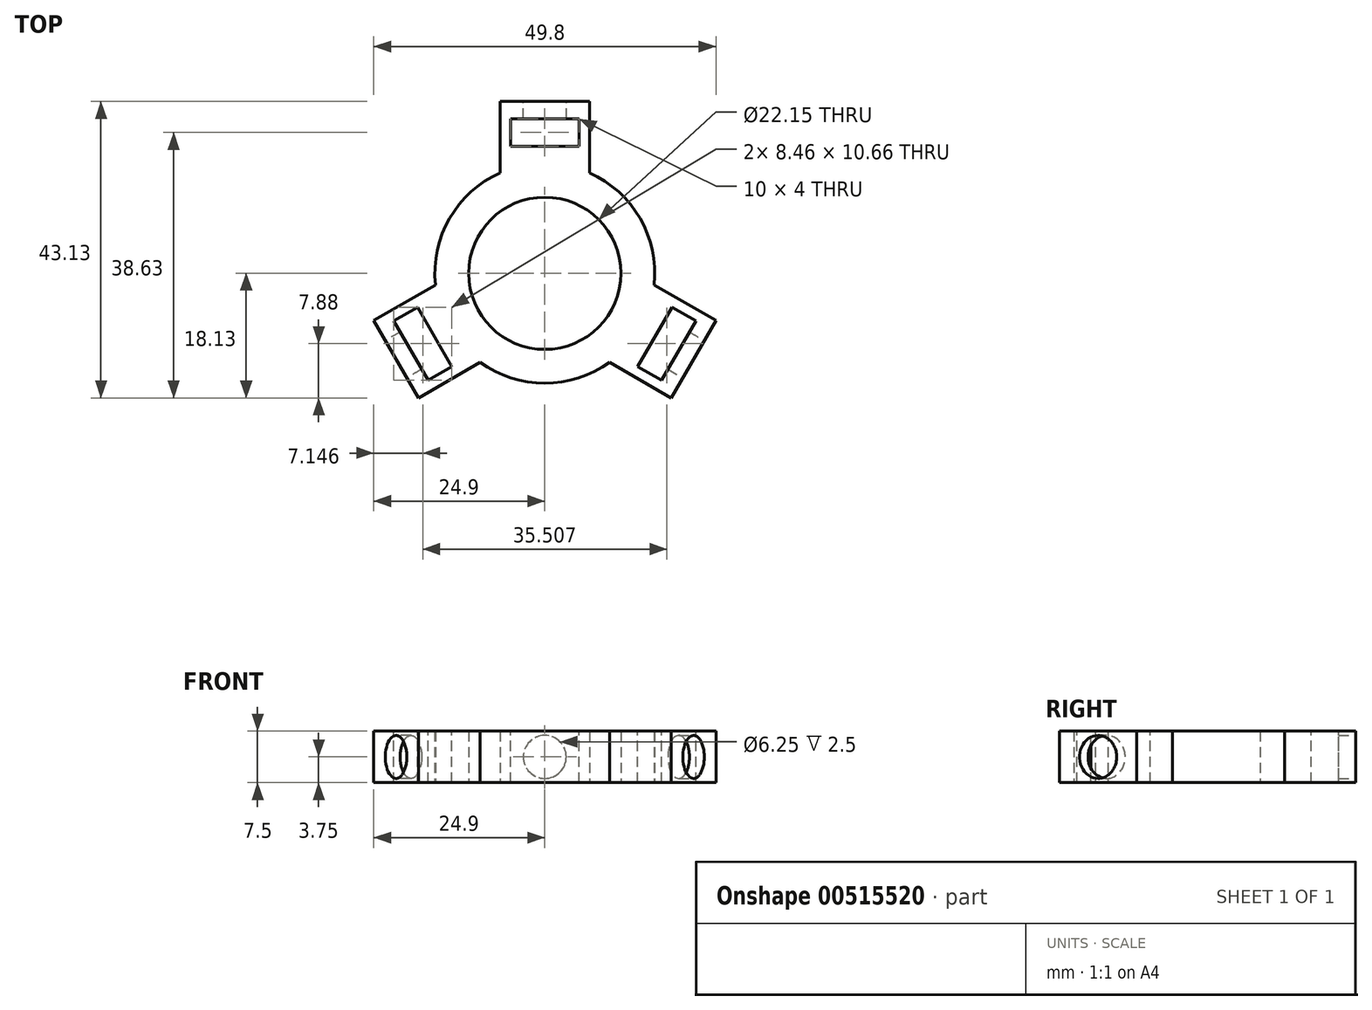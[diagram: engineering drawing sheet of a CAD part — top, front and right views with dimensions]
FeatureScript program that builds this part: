
annotation { "Feature Type Name" : "Feature", "Feature Type Description" : "" }
export const myFeature = defineFeature(function(context is Context, id is Id, definition is map)
    precondition{}
    {
        {
            var Q0;
            Q0=qCreatedBy(makeId("Top.planeOp"),FACE);
            var sketch = newSketch(context, id + "F0", { "sketchPlane" : qUnion([Q0])});
            skCircle(sketch, "E0", {"center": v(0, 0) * mm, "radius": 11.07 * mm});
            skCircle(sketch, "E1", {"center": v(0, 0) * mm, "radius": 16 * mm});
            skLineSegment(sketch, "E2", {"start": v(0, 0) * mm, "end": v(0, 25) * mm});
            skLineSegment(sketch, "E3", {"start": v(0, 25) * mm, "end": v(6.5, 25) * mm});
            skLineSegment(sketch, "E4", {"start": v(6.5, 25) * mm, "end": v(6.5, 14.62) * mm});
            skLineSegment(sketch, "E5", {"start": v(0, 25) * mm, "end": v(-6.5, 25) * mm});
            skLineSegment(sketch, "E6", {"start": v(-6.5, 25) * mm, "end": v(-6.5, 14.62) * mm});
            skLineSegment(sketch, "E7", {"start": v(0, 0) * mm, "end": v(21.65, -12.5) * mm});
            skLineSegment(sketch, "E8", {"start": v(0, 0) * mm, "end": v(-21.65, -12.5) * mm});
            skLineSegment(sketch, "E9", {"start": v(21.65, -12.5) * mm, "end": v(24.9, -6.87) * mm});
            skLineSegment(sketch, "E10", {"start": v(24.9, -6.87) * mm, "end": v(15.91, -1.68) * mm});
            skLineSegment(sketch, "E11", {"start": v(21.65, -12.5) * mm, "end": v(18.4, -18.13) * mm});
            skLineSegment(sketch, "E12", {"start": v(18.4, -18.13) * mm, "end": v(9.41, -12.94) * mm});
            skLineSegment(sketch, "E13", {"start": v(-21.65, -12.5) * mm, "end": v(-18.4, -18.13) * mm});
            skLineSegment(sketch, "E14", {"start": v(-18.4, -18.13) * mm, "end": v(-9.41, -12.94) * mm});
            skLineSegment(sketch, "E15", {"start": v(-21.65, -12.5) * mm, "end": v(-24.9, -6.87) * mm});
            skLineSegment(sketch, "E16", {"start": v(-24.9, -6.87) * mm, "end": v(-15.91, -1.68) * mm});
            skSolve(sketch);
        }
        {
            var Q0;
            {var subQ2=sQuery(id+"F0.wireOp",EDGE,"E8");var subQ7=sQuery(id+"F0.wireOp",EDGE,"E0");var subQ8=makeQuery(id+"F0.imprint","INTERSECT",VERTEX,{"derivedFrom":[subQ7,subQ2]});Q0=makeQuery(id+"F0.imprint","IMPRINT",FACE,{"disambiguationData":[TD([[makeQuery(id+"F0.imprint","IMPRINT",EDGE,{"disambiguationData":[TD([[subQ8,1.0]])],"derivedFrom":subQ7}),-1.0]])]});}
            var Q1;
            {var subQ5=sQuery(id+"F0.wireOp",EDGE,"E2");var subQ7=sQuery(id+"F0.wireOp",EDGE,"E0");var subQ8=makeQuery(id+"F0.imprint","INTERSECT",VERTEX,{"derivedFrom":[subQ7,subQ5]});Q1=makeQuery(id+"F0.imprint","IMPRINT",FACE,{"disambiguationData":[TD([[makeQuery(id+"F0.imprint","IMPRINT",EDGE,{"disambiguationData":[TD([[subQ8,1.0]])],"derivedFrom":subQ7}),-1.0]])]});}
            var Q2;
            {var subQ4=sQuery(id+"F0.wireOp",EDGE,"E0");var subQ7=sQuery(id+"F0.wireOp",EDGE,"E8");var subQ9=makeQuery(id+"F0.imprint","INTERSECT",VERTEX,{"derivedFrom":[subQ4,subQ7]});Q2=makeQuery(id+"F0.imprint","IMPRINT",FACE,{"disambiguationData":[TD([[makeQuery(id+"F0.imprint","IMPRINT",EDGE,{"disambiguationData":[TD([[subQ9,-1.0]])],"derivedFrom":subQ4}),-1.0]])]});}
            var Q3;
            {var subQ4=sQuery(id+"F0.wireOp",EDGE,"E3");Q3=makeQuery(id+"F0.imprint","IMPRINT",FACE,{"disambiguationData":[TD([[makeQuery(id+"F0.imprint","IMPRINT",EDGE,{"derivedFrom":subQ4}),-1.0]])]});}
            var Q4;
            {var subQ4=sQuery(id+"F0.wireOp",EDGE,"E5");Q4=makeQuery(id+"F0.imprint","IMPRINT",FACE,{"disambiguationData":[TD([[makeQuery(id+"F0.imprint","IMPRINT",EDGE,{"derivedFrom":subQ4}),1.0]])]});}
            var Q5;
            {var subQ4=sQuery(id+"F0.wireOp",EDGE,"E15");Q5=makeQuery(id+"F0.imprint","IMPRINT",FACE,{"disambiguationData":[TD([[makeQuery(id+"F0.imprint","IMPRINT",EDGE,{"derivedFrom":subQ4}),-1.0]])]});}
            var Q6;
            {var subQ4=sQuery(id+"F0.wireOp",EDGE,"E13");Q6=makeQuery(id+"F0.imprint","IMPRINT",FACE,{"disambiguationData":[TD([[makeQuery(id+"F0.imprint","IMPRINT",EDGE,{"derivedFrom":subQ4}),1.0]])]});}
            var Q7;
            {var subQ4=sQuery(id+"F0.wireOp",EDGE,"E11");Q7=makeQuery(id+"F0.imprint","IMPRINT",FACE,{"disambiguationData":[TD([[makeQuery(id+"F0.imprint","IMPRINT",EDGE,{"derivedFrom":subQ4}),-1.0]])]});}
            var Q8;
            {var subQ4=sQuery(id+"F0.wireOp",EDGE,"E9");Q8=makeQuery(id+"F0.imprint","IMPRINT",FACE,{"disambiguationData":[TD([[makeQuery(id+"F0.imprint","IMPRINT",EDGE,{"derivedFrom":subQ4}),1.0]])]});}
            extrude(context, id + "F1", {"entities" : qUnion([Q0, Q1, Q2, Q3, Q4, Q5, Q6, Q7, Q8]), "depth" : 7.5 * mm, "offsetDistance" : 25 * mm});
        }
        {
            var Q0;
            Q0=makeQuery(id+"F1.opExtrude","CAP_FACE",FACE,{"disambiguationData":[OSD([sQuery(id+"F0.wireOp",EDGE,"E0"),sQuery(id+"F0.wireOp",EDGE,"E1"),sQuery(id+"F0.wireOp",EDGE,"E3"),sQuery(id+"F0.wireOp",EDGE,"E4"),sQuery(id+"F0.wireOp",EDGE,"E5"),sQuery(id+"F0.wireOp",EDGE,"E6"),sQuery(id+"F0.wireOp",EDGE,"E9"),sQuery(id+"F0.wireOp",EDGE,"E10"),sQuery(id+"F0.wireOp",EDGE,"E11"),sQuery(id+"F0.wireOp",EDGE,"E12"),sQuery(id+"F0.wireOp",EDGE,"E13"),sQuery(id+"F0.wireOp",EDGE,"E14"),sQuery(id+"F0.wireOp",EDGE,"E15"),sQuery(id+"F0.wireOp",EDGE,"E16")])],"isStart":false});
            var sketch = newSketch(context, id + "F2", { "sketchPlane" : qUnion([Q0])});
            skLineSegment(sketch, "E17", {"start": v(0, 25) * mm, "end": v(0, 22.5) * mm});
            skLineSegment(sketch, "E18", {"start": v(0, 22.5) * mm, "end": v(5, 22.5) * mm});
            skLineSegment(sketch, "E19", {"start": v(5, 22.5) * mm, "end": v(5, 18.5) * mm});
            skLineSegment(sketch, "E20", {"start": v(5, 18.5) * mm, "end": v(-5, 18.5) * mm});
            skLineSegment(sketch, "E21", {"start": v(-5, 18.5) * mm, "end": v(-5, 22.5) * mm});
            skLineSegment(sketch, "E22", {"start": v(-5, 22.5) * mm, "end": v(0, 22.5) * mm});
            skLineSegment(sketch, "E23", {"start": v(0, 0) * mm, "end": v(21.65, -12.5) * mm});
            skLineSegment(sketch, "E24", {"start": v(21.65, -12.5) * mm, "end": v(19.49, -11.25) * mm});
            skLineSegment(sketch, "E25", {"start": v(19.49, -11.25) * mm, "end": v(21.99, -6.92) * mm});
            skLineSegment(sketch, "E26", {"start": v(21.99, -6.92) * mm, "end": v(18.52, -4.92) * mm});
            skLineSegment(sketch, "E27", {"start": v(18.52, -4.92) * mm, "end": v(13.52, -13.58) * mm});
            skLineSegment(sketch, "E28", {"start": v(13.52, -13.58) * mm, "end": v(16.99, -15.58) * mm});
            skLineSegment(sketch, "E29", {"start": v(16.99, -15.58) * mm, "end": v(19.49, -11.25) * mm});
            skLineSegment(sketch, "E30", {"start": v(0, 0) * mm, "end": v(-21.65, -12.5) * mm});
            skLineSegment(sketch, "E31", {"start": v(-21.65, -12.5) * mm, "end": v(-19.49, -11.25) * mm});
            skLineSegment(sketch, "E32", {"start": v(-19.49, -11.25) * mm, "end": v(-21.99, -6.92) * mm});
            skLineSegment(sketch, "E33", {"start": v(-19.49, -11.25) * mm, "end": v(-16.99, -15.58) * mm});
            skLineSegment(sketch, "E34", {"start": v(-16.99, -15.58) * mm, "end": v(-13.52, -13.58) * mm});
            skLineSegment(sketch, "E35", {"start": v(-13.52, -13.58) * mm, "end": v(-18.52, -4.92) * mm});
            skLineSegment(sketch, "E36", {"start": v(-18.52, -4.92) * mm, "end": v(-21.99, -6.92) * mm});
            skSolve(sketch);
        }
        {
            var Q0;
            Q0=makeQuery(id+"F2.imprint","IMPRINT",FACE,{"disambiguationData":[TD([[makeQuery(id+"F2.imprint","IMPRINT",EDGE,{"derivedFrom":sQuery(id+"F2.wireOp",EDGE,"E18")}),-1.0]])]});
            var Q1;
            {var subQ0=sQuery(id+"F2.wireOp",EDGE,"E32");Q1=makeQuery(id+"F2.imprint","IMPRINT",FACE,{"disambiguationData":[TD([[makeQuery(id+"F2.imprint","IMPRINT",EDGE,{"derivedFrom":subQ0}),-1.0]])]});}
            var Q2;
            {var subQ0=sQuery(id+"F2.wireOp",EDGE,"E33");Q2=makeQuery(id+"F2.imprint","IMPRINT",FACE,{"disambiguationData":[TD([[makeQuery(id+"F2.imprint","IMPRINT",EDGE,{"derivedFrom":subQ0}),1.0]])]});}
            var Q3;
            {var subQ4=sQuery(id+"F2.wireOp",EDGE,"E28");Q3=makeQuery(id+"F2.imprint","IMPRINT",FACE,{"disambiguationData":[TD([[makeQuery(id+"F2.imprint","IMPRINT",EDGE,{"derivedFrom":subQ4}),1.0]])]});}
            var Q4;
            {var subQ0=sQuery(id+"F2.wireOp",EDGE,"E25");Q4=makeQuery(id+"F2.imprint","IMPRINT",FACE,{"disambiguationData":[TD([[makeQuery(id+"F2.imprint","IMPRINT",EDGE,{"derivedFrom":subQ0}),1.0]])]});}
            extrude(context, id + "F3", {"entities" : qUnion([Q0, Q1, Q2, Q3, Q4]), "operationType" : NewBodyOperationType.REMOVE, "oppositeDirection" : true, "depth" : 25 * mm, "offsetDistance" : 25 * mm});
        }
        {
            var Q0;
            Q0=makeQuery(id+"F1.opExtrude","SWEPT_FACE",FACE,{"disambiguationData":[OSD([sQuery(id+"F0.wireOp",EDGE,"E13"),sQuery(id+"F0.wireOp",EDGE,"E15")])]});
            var sketch = newSketch(context, id + "F4", { "sketchPlane" : qUnion([Q0])});
            skLineSegment(sketch, "E37", {"start": v(0, 0) * mm, "end": v(0, 7.5) * mm});
            skCircle(sketch, "E38", {"center": v(0, 3.75) * mm, "radius": 3.12 * mm});
            skSolve(sketch);
        }
        {
            var Q0;
            {var subQ0=sQuery(id+"F4.wireOp",EDGE,"E38");var subQ1=sQuery(id+"F4.wireOp",EDGE,"E37");var subQ2=makeQuery(id+"F4.imprint","INTERSECT",VERTEX,{"disambiguationData":[OD(0.0)],"derivedFrom":[subQ1,subQ0]});Q0=makeQuery(id+"F4.imprint","IMPRINT",FACE,{"disambiguationData":[TD([[makeQuery(id+"F4.imprint","IMPRINT",EDGE,{"disambiguationData":[TD([[subQ2,-1.0]])],"derivedFrom":subQ1}),1.0]])]});}
            var Q1;
            {var subQ0=sQuery(id+"F4.wireOp",EDGE,"E38");var subQ1=sQuery(id+"F4.wireOp",EDGE,"E37");var subQ2=makeQuery(id+"F4.imprint","INTERSECT",VERTEX,{"disambiguationData":[OD(0.0)],"derivedFrom":[subQ1,subQ0]});Q1=makeQuery(id+"F4.imprint","IMPRINT",FACE,{"disambiguationData":[TD([[makeQuery(id+"F4.imprint","IMPRINT",EDGE,{"disambiguationData":[TD([[subQ2,-1.0]])],"derivedFrom":subQ1}),-1.0]])]});}
            extrude(context, id + "F5", {"entities" : qUnion([Q0, Q1]), "operationType" : NewBodyOperationType.REMOVE, "oppositeDirection" : true, "depth" : 6 * mm, "offsetDistance" : 25 * mm});
        }
        {
            var Q0;
            Q0=makeQuery(id+"F1.opExtrude","SWEPT_FACE",FACE,{"disambiguationData":[OSD([sQuery(id+"F0.wireOp",EDGE,"E3"),sQuery(id+"F0.wireOp",EDGE,"E5")])]});
            var sketch = newSketch(context, id + "F6", { "sketchPlane" : qUnion([Q0])});
            skLineSegment(sketch, "E39", {"start": v(0, 0) * mm, "end": v(0, 7.5) * mm});
            skCircle(sketch, "E40", {"center": v(0, 3.75) * mm, "radius": 3.12 * mm});
            skSolve(sketch);
        }
        {
            var Q0;
            {var subQ0=sQuery(id+"F6.wireOp",EDGE,"E40");var subQ1=sQuery(id+"F6.wireOp",EDGE,"E39");var subQ2=makeQuery(id+"F6.imprint","INTERSECT",VERTEX,{"disambiguationData":[OD(0.0)],"derivedFrom":[subQ1,subQ0]});Q0=makeQuery(id+"F6.imprint","IMPRINT",FACE,{"disambiguationData":[TD([[makeQuery(id+"F6.imprint","IMPRINT",EDGE,{"disambiguationData":[TD([[subQ2,-1.0]])],"derivedFrom":subQ1}),-1.0]])]});}
            var Q1;
            {var subQ0=sQuery(id+"F6.wireOp",EDGE,"E40");var subQ1=sQuery(id+"F6.wireOp",EDGE,"E39");var subQ2=makeQuery(id+"F6.imprint","INTERSECT",VERTEX,{"disambiguationData":[OD(0.0)],"derivedFrom":[subQ1,subQ0]});Q1=makeQuery(id+"F6.imprint","IMPRINT",FACE,{"disambiguationData":[TD([[makeQuery(id+"F6.imprint","IMPRINT",EDGE,{"disambiguationData":[TD([[subQ2,-1.0]])],"derivedFrom":subQ1}),1.0]])]});}
            extrude(context, id + "F7", {"entities" : qUnion([Q0, Q1]), "operationType" : NewBodyOperationType.REMOVE, "oppositeDirection" : true, "depth" : 6 * mm, "offsetDistance" : 25 * mm});
        }
        {
            var Q0;
            Q0=makeQuery(id+"F1.opExtrude","SWEPT_FACE",FACE,{"disambiguationData":[OSD([sQuery(id+"F0.wireOp",EDGE,"E9"),sQuery(id+"F0.wireOp",EDGE,"E11")])]});
            var sketch = newSketch(context, id + "F8", { "sketchPlane" : qUnion([Q0])});
            skLineSegment(sketch, "E41", {"start": v(0, 7.5) * mm, "end": v(0, 0) * mm});
            skCircle(sketch, "E42", {"center": v(0, 3.75) * mm, "radius": 3.12 * mm});
            skSolve(sketch);
        }
        {
            var Q0;
            {var subQ0=sQuery(id+"F8.wireOp",EDGE,"E42");var subQ1=sQuery(id+"F8.wireOp",EDGE,"E41");var subQ2=makeQuery(id+"F8.imprint","INTERSECT",VERTEX,{"disambiguationData":[OD(0.0)],"derivedFrom":[subQ1,subQ0]});Q0=makeQuery(id+"F8.imprint","IMPRINT",FACE,{"disambiguationData":[TD([[makeQuery(id+"F8.imprint","IMPRINT",EDGE,{"disambiguationData":[TD([[subQ2,-1.0]])],"derivedFrom":subQ1}),1.0]])]});}
            var Q1;
            {var subQ0=sQuery(id+"F8.wireOp",EDGE,"E42");var subQ1=sQuery(id+"F8.wireOp",EDGE,"E41");var subQ2=makeQuery(id+"F8.imprint","INTERSECT",VERTEX,{"disambiguationData":[OD(0.0)],"derivedFrom":[subQ1,subQ0]});Q1=makeQuery(id+"F8.imprint","IMPRINT",FACE,{"disambiguationData":[TD([[makeQuery(id+"F8.imprint","IMPRINT",EDGE,{"disambiguationData":[TD([[subQ2,-1.0]])],"derivedFrom":subQ1}),-1.0]])]});}
            extrude(context, id + "F9", {"entities" : qUnion([Q0, Q1]), "operationType" : NewBodyOperationType.REMOVE, "oppositeDirection" : true, "depth" : 6 * mm, "offsetDistance" : 25 * mm});
        }
    });
